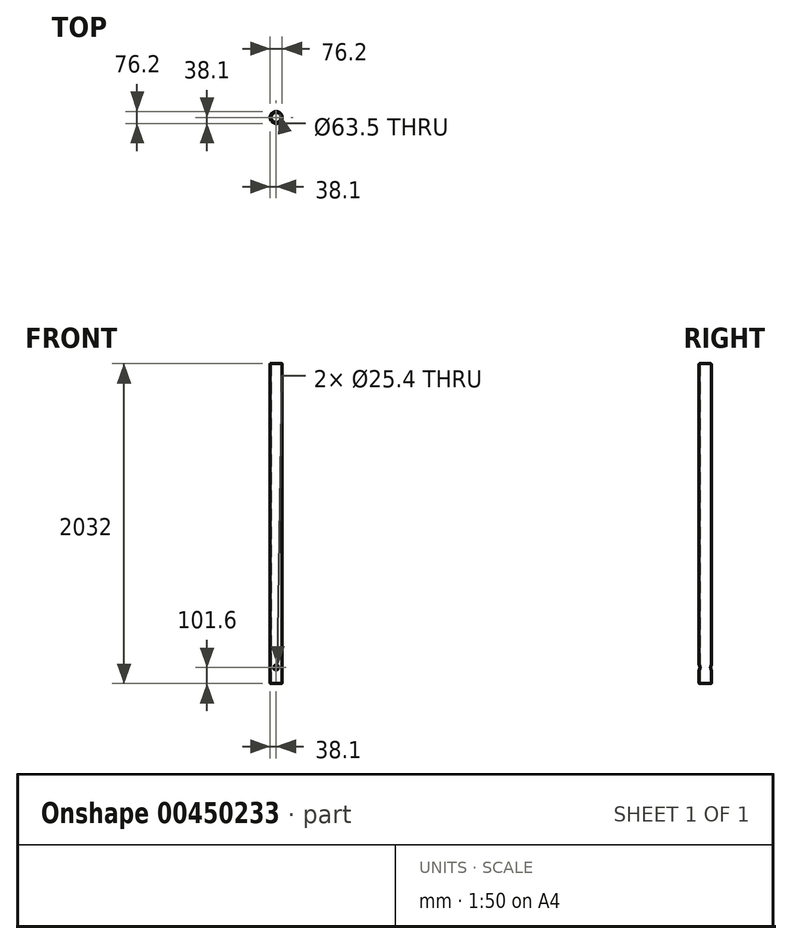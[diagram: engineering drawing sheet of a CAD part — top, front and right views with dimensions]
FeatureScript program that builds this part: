
annotation { "Feature Type Name" : "Feature", "Feature Type Description" : "" }
export const myFeature = defineFeature(function(context is Context, id is Id, definition is map)
    precondition{}
    {
        {
            var Q0;
            Q0=qCreatedBy(makeId("Top.planeOp"),FACE);
            var sketch = newSketch(context, id + "F0", { "sketchPlane" : qUnion([Q0])});
            skCircle(sketch, "E0", {"center": v(0, 0) * mm, "radius": 31.75 * mm});
            skCircle(sketch, "E1.0", {"center": v(0, 0) * mm, "radius": 38.1 * mm});
            skSolve(sketch);
        }
        {
            var Q0;
            Q0=makeQuery(id+"F0.imprint","IMPRINT",FACE,{"disambiguationData":[TD([[makeQuery(id+"F0.imprint","IMPRINT",EDGE,{"derivedFrom":sQuery(id+"F0.wireOp",EDGE,"E0")}),-1.0]])]});
            extrude(context, id + "F1", {"entities" : qUnion([Q0]), "depth" : 2032 * mm});
        }
        {
            var Q0;
            Q0=qCreatedBy(makeId("Front.planeOp"),FACE);
            var sketch = newSketch(context, id + "F2", { "sketchPlane" : qUnion([Q0])});
            skCircle(sketch, "E2", {"center": v(0, 101.6) * mm, "radius": 12.7 * mm});
            skLineSegment(sketch, "E3", {"start": v(-38.1, 0) * mm, "end": v(-38.1, 2032) * mm});
            skLineSegment(sketch, "E4", {"start": v(38.1, 2032) * mm, "end": v(38.1, 0) * mm});
            skSolve(sketch);
        }
        {
            var Q0;
            Q0 = qSketchRegion(id + "F2", true);
            extrude(context, id + "F3", {"entities" : qUnion([Q0]), "operationType" : NewBodyOperationType.REMOVE, "endBound" : BoundingType.THROUGH_ALL, "depth" : 76.2 * mm, "hasSecondDirection" : true, "secondDirectionBound" : SecondDirectionBoundingType.THROUGH_ALL, "secondDirectionOppositeDirection" : true, "secondDirectionDepth" : 25.4 * mm});
        }
        {
            var Q0;
            Q0=makeQuery(id+"F3.boolean.opBoolean","INTERSECT",EDGE,{"disambiguationData":[OD(1.0)],"derivedFrom":[makeQuery(id+"F1.opExtrude","SWEPT_FACE",FACE,{"disambiguationData":[OSD([sQuery(id+"F0.wireOp",EDGE,"E1.0")])]}),makeQuery(id+"F3.opExtrude","SWEPT_FACE",FACE,{"disambiguationData":[OSD([sQuery(id+"F2.wireOp",EDGE,"E2")])]})]});
            var Q1;
            Q1=makeQuery(id+"F1.opExtrude","SWEPT_FACE",FACE,{"disambiguationData":[OSD([sQuery(id+"F0.wireOp",EDGE,"E1.0")])]});
            var Q2;
            Q2=makeQuery(id+"F3.boolean.opBoolean","INTERSECT",EDGE,{"disambiguationData":[OD(0.0)],"derivedFrom":[makeQuery(id+"F1.opExtrude","SWEPT_FACE",FACE,{"disambiguationData":[OSD([sQuery(id+"F0.wireOp",EDGE,"E0")])]}),makeQuery(id+"F3.opExtrude","SWEPT_FACE",FACE,{"disambiguationData":[OSD([sQuery(id+"F2.wireOp",EDGE,"E2")])]})]});
            var Q3;
            Q3=makeQuery(id+"F1.opExtrude","CAP_EDGE",EDGE,{"disambiguationData":[OSD([sQuery(id+"F0.wireOp",EDGE,"E0")])],"isStart":true});
            var Q4;
            Q4=makeQuery(id+"F1.opExtrude","CAP_EDGE",EDGE,{"disambiguationData":[OSD([sQuery(id+"F0.wireOp",EDGE,"E1.0")])],"isStart":true});
            var Q5;
            Q5=makeQuery(id+"F1.opExtrude","CAP_EDGE",EDGE,{"disambiguationData":[OSD([sQuery(id+"F0.wireOp",EDGE,"E0")])],"isStart":false});
            var Q6;
            Q6=makeQuery(id+"F1.opExtrude","CAP_EDGE",EDGE,{"disambiguationData":[OSD([sQuery(id+"F0.wireOp",EDGE,"E1.0")])],"isStart":false});
            var Q7;
            Q7=makeQuery(id+"F3.boolean.opBoolean","INTERSECT",EDGE,{"disambiguationData":[OD(1.0)],"derivedFrom":[makeQuery(id+"F1.opExtrude","SWEPT_FACE",FACE,{"disambiguationData":[OSD([sQuery(id+"F0.wireOp",EDGE,"E0")])]}),makeQuery(id+"F3.opExtrude","SWEPT_FACE",FACE,{"disambiguationData":[OSD([sQuery(id+"F2.wireOp",EDGE,"E2")])]})]});
            fillet(context, id + "F4", {"entities" : qUnion([Q0, Q1, Q2, Q3, Q4, Q5, Q6, Q7]), "radius" : 2.54 * mm, "allowEdgeOverflow" : false});
        }
    });
